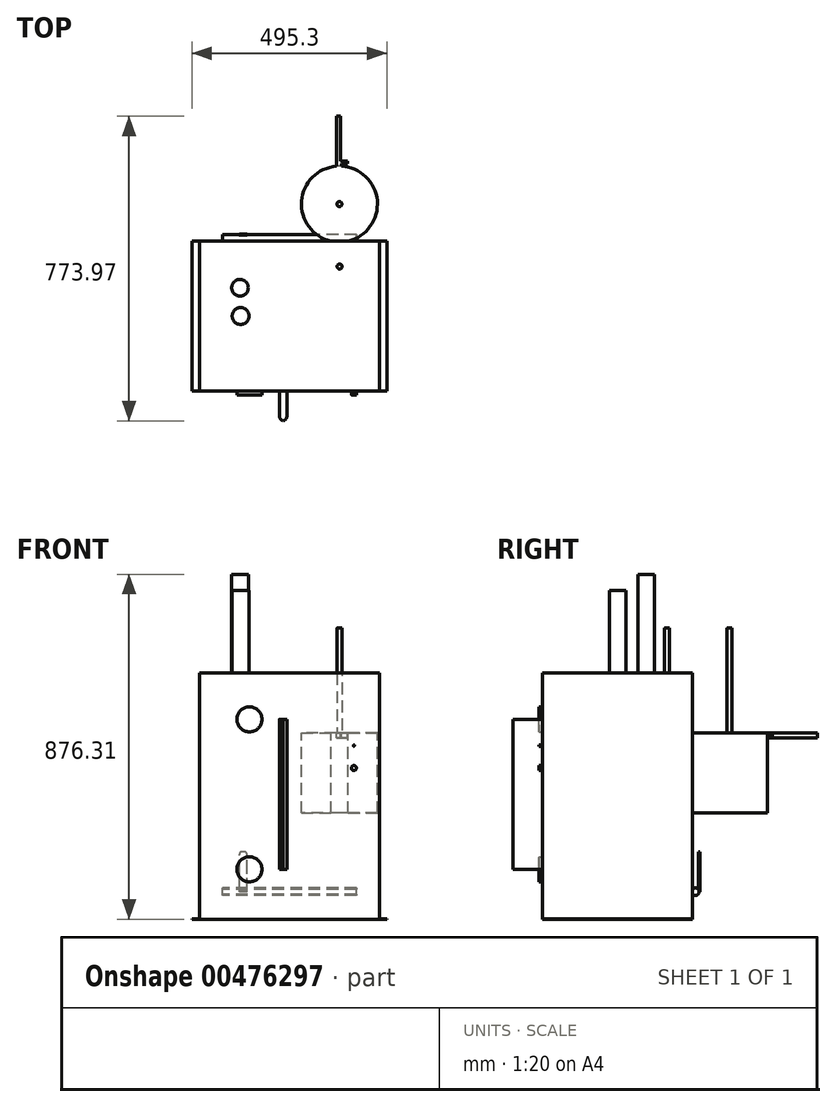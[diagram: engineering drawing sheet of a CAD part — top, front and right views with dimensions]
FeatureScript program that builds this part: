
annotation { "Feature Type Name" : "Feature", "Feature Type Description" : "" }
export const myFeature = defineFeature(function(context is Context, id is Id, definition is map)
    precondition{}
    {
        {
            var Q0;
            Q0=qCreatedBy(makeId("Top.planeOp"),FACE);
            var sketch = newSketch(context, id + "F0", { "sketchPlane" : qUnion([Q0])});
            skLineSegment(sketch, "E0.bottom", {"start": v(-228.6, 190.5) * mm, "end": v(228.6, 190.5) * mm});
            skLineSegment(sketch, "E0.top", {"start": v(-228.6, -190.5) * mm, "end": v(228.6, -190.5) * mm});
            skLineSegment(sketch, "E0.left", {"start": v(-228.6, 190.5) * mm, "end": v(-228.6, -190.5) * mm});
            skLineSegment(sketch, "E0.right", {"start": v(228.6, 190.5) * mm, "end": v(228.6, -190.5) * mm});
            skLineSegment(sketch, "E1", {"start": v(-228.6, 0) * mm, "end": v(228.6, 0) * mm, "construction": true});
            skPoint(sketch, "E2", {"position": v(0, 0) * mm});
            skSolve(sketch);
        }
        {
            var Q0;
            Q0 = qSketchRegion(id + "F0", true);
            extrude(context, id + "F1", {"entities" : qUnion([Q0]), "oppositeDirection" : true, "depth" : 625.47 * mm, "offsetDistance" : 25.4 * mm});
        }
        {
            var Q0;
            Q0=makeQuery(id+"F1.opExtrude","CAP_FACE",FACE,{"disambiguationData":[OSD([sQuery(id+"F0.wireOp",EDGE,"E0.bottom"),sQuery(id+"F0.wireOp",EDGE,"E0.top"),sQuery(id+"F0.wireOp",EDGE,"E0.left"),sQuery(id+"F0.wireOp",EDGE,"E0.right")])],"isStart":true});
            var sketch = newSketch(context, id + "F2", { "sketchPlane" : qUnion([Q0])});
            skCircle(sketch, "E3", {"center": v(-125.47, 72) * mm, "radius": 21.1 * mm});
            skSolve(sketch);
        }
        {
            var Q0;
            Q0 = qSketchRegion(id + "F2", true);
            extrude(context, id + "F3", {"entities" : qUnion([Q0]), "operationType" : NewBodyOperationType.ADD, "depth" : 250.82 * mm, "offsetDistance" : 25.4 * mm});
        }
        {
            var Q0;
            Q0=makeQuery(id+"F1.opExtrude","CAP_FACE",FACE,{"disambiguationData":[OSD([sQuery(id+"F0.wireOp",EDGE,"E0.bottom"),sQuery(id+"F0.wireOp",EDGE,"E0.top"),sQuery(id+"F0.wireOp",EDGE,"E0.left"),sQuery(id+"F0.wireOp",EDGE,"E0.right")])],"isStart":true});
            var sketch = newSketch(context, id + "F4", { "sketchPlane" : qUnion([Q0])});
            skCircle(sketch, "E4", {"center": v(-124.02, 0) * mm, "radius": 21.4 * mm});
            skSolve(sketch);
        }
        {
            var Q0;
            Q0 = qSketchRegion(id + "F4", true);
            extrude(context, id + "F5", {"entities" : qUnion([Q0]), "operationType" : NewBodyOperationType.ADD, "depth" : 209.55 * mm, "offsetDistance" : 25.4 * mm});
        }
        {
            var Q0;
            Q0=makeQuery(id+"F1.opExtrude","SWEPT_FACE",FACE,{"disambiguationData":[OSD([sQuery(id+"F0.wireOp",EDGE,"E0.top")])]});
            var sketch = newSketch(context, id + "F6", { "sketchPlane" : qUnion([Q0])});
            skCircle(sketch, "E5", {"center": v(-101.6, -117.48) * mm, "radius": 31.75 * mm});
            skCircle(sketch, "E6", {"center": v(-101.6, -498.48) * mm, "radius": 31.75 * mm});
            skCircle(sketch, "E7", {"center": v(163.79, -184.2) * mm, "radius": 1.59 * mm});
            skLineSegment(sketch, "E8", {"start": v(163.79, -184.2) * mm, "end": v(163.79, -241.12) * mm, "construction": true});
            skCircle(sketch, "E9", {"center": v(163.79, -241.12) * mm, "radius": 6.35 * mm});
            skSolve(sketch);
        }
        {
            var Q0;
            Q0 = qSketchRegion(id + "F6", true);
            extrude(context, id + "F7", {"entities" : qUnion([Q0]), "operationType" : NewBodyOperationType.ADD, "depth" : 9.52 * mm, "offsetDistance" : 25.4 * mm});
        }
        {
            var Q0;
            Q0=makeQuery(id+"F1.opExtrude","SWEPT_FACE",FACE,{"disambiguationData":[OSD([sQuery(id+"F0.wireOp",EDGE,"E0.top")])]});
            var sketch = newSketch(context, id + "F8", { "sketchPlane" : qUnion([Q0])});
            skLineSegment(sketch, "E10.bottom", {"start": v(-25.4, -117.48) * mm, "end": v(-6.35, -117.48) * mm});
            skLineSegment(sketch, "E10.top", {"start": v(-25.4, -498.48) * mm, "end": v(-6.35, -498.48) * mm});
            skLineSegment(sketch, "E10.left", {"start": v(-25.4, -117.48) * mm, "end": v(-25.4, -498.48) * mm});
            skLineSegment(sketch, "E10.right", {"start": v(-6.35, -117.48) * mm, "end": v(-6.35, -498.48) * mm});
            skPoint(sketch, "E11", {"position": v(-101.6, -117.48) * mm});
            skPoint(sketch, "E12", {"position": v(-101.6, -498.48) * mm});
            skSolve(sketch);
        }
        {
            var Q0;
            Q0 = qSketchRegion(id + "F8", true);
            extrude(context, id + "F9", {"entities" : qUnion([Q0]), "operationType" : NewBodyOperationType.ADD, "depth" : 76.2 * mm, "offsetDistance" : 25.4 * mm});
        }
        {
            var Q0;
            Q0=makeQuery(id+"F9.opExtrude","CAP_EDGE",EDGE,{"disambiguationData":[OSD([sQuery(id+"F8.wireOp",EDGE,"E10.left")])],"isStart":false});
            var Q1;
            Q1=makeQuery(id+"F9.opExtrude","CAP_EDGE",EDGE,{"disambiguationData":[OSD([sQuery(id+"F8.wireOp",EDGE,"E10.right")])],"isStart":false});
            fillet(context, id + "F10", {"entities" : qUnion([Q0, Q1]), "radius" : 12.7 * mm, "tangentPropagation" : true, "allowEdgeOverflow" : false});
        }
        {
            var Q0;
            Q0=qCreatedBy(makeId("Top.planeOp"),FACE);
            cPlane(context, id + "F11", {"entities" : qUnion([Q0]), "cplaneType" : CPlaneType.OFFSET, "offset" : 152.4 * mm, "oppositeDirection" : true, "width" : 152.4 * mm, "height" : 152.4 * mm});
        }
        {
            var Q0;
            Q0=qCreatedBy(id+"F11.planeOp",FACE);
            var sketch = newSketch(context, id + "F12", { "sketchPlane" : qUnion([Q0])});
            skCircle(sketch, "E13", {"center": v(127.07, 284.48) * mm, "radius": 96.52 * mm});
            skLineSegment(sketch, "E14", {"start": v(127.07, 381) * mm, "end": v(127.07, 187.96) * mm, "construction": true});
            skSolve(sketch);
        }
        {
            var Q0;
            Q0 = qSketchRegion(id + "F12", true);
            extrude(context, id + "F13", {"entities" : qUnion([Q0]), "operationType" : NewBodyOperationType.ADD, "oppositeDirection" : true, "depth" : 203.2 * mm, "offsetDistance" : 25.4 * mm});
        }
        {
            var Q0;
            Q0=makeQuery(id+"F13.opExtrude","CAP_FACE",FACE,{"disambiguationData":[OSD([sQuery(id+"F12.wireOp",EDGE,"E13")])],"isStart":true});
            var sketch = newSketch(context, id + "F14", { "sketchPlane" : qUnion([Q0])});
            skLineSegment(sketch, "E15", {"start": v(119.09, 380.67) * mm, "end": v(119.09, 393.37) * mm});
            skLineSegment(sketch, "E16", {"start": v(129.25, 393.37) * mm, "end": v(147.66, 393.37) * mm});
            skLineSegment(sketch, "E17", {"start": v(147.66, 393.37) * mm, "end": v(147.66, 387.02) * mm});
            skLineSegment(sketch, "E18", {"start": v(147.66, 387.02) * mm, "end": v(131.79, 387.02) * mm});
            skLineSegment(sketch, "E19", {"start": v(131.79, 387.02) * mm, "end": v(131.79, 380.88) * mm});
            skLineSegment(sketch, "E20", {"start": v(119.09, 380.67) * mm, "end": v(131.79, 380.88) * mm});
            skLineSegment(sketch, "E21", {"start": v(119.09, 393.37) * mm, "end": v(119.09, 507.67) * mm});
            skLineSegment(sketch, "E22", {"start": v(119.09, 507.67) * mm, "end": v(129.25, 507.67) * mm});
            skLineSegment(sketch, "E23", {"start": v(129.25, 507.67) * mm, "end": v(129.25, 393.37) * mm});
            skSolve(sketch);
        }
        {
            var Q0;
            Q0 = qSketchRegion(id + "F14", true);
            extrude(context, id + "F15", {"entities" : qUnion([Q0]), "operationType" : NewBodyOperationType.ADD, "oppositeDirection" : true, "depth" : 12.7 * mm, "offsetDistance" : 25.4 * mm});
        }
        {
            var Q0;
            Q0=makeQuery(id+"F15.boolean.opBoolean","MERGE",FACE,{"derivedFrom":[makeQuery(id+"F13.opExtrude","CAP_FACE",FACE,{"disambiguationData":[OSD([sQuery(id+"F12.wireOp",EDGE,"E13")])],"isStart":true}),makeQuery(id+"F15.opExtrude","CAP_FACE",FACE,{"disambiguationData":[OSD([sQuery(id+"F14.wireOp",EDGE,"E15"),sQuery(id+"F14.wireOp",EDGE,"E16"),sQuery(id+"F14.wireOp",EDGE,"E17"),sQuery(id+"F14.wireOp",EDGE,"E18"),sQuery(id+"F14.wireOp",EDGE,"E19"),sQuery(id+"F14.wireOp",EDGE,"E20"),sQuery(id+"F14.wireOp",EDGE,"E21"),sQuery(id+"F14.wireOp",EDGE,"E22"),sQuery(id+"F14.wireOp",EDGE,"E23")])],"isStart":true})]});
            var sketch = newSketch(context, id + "F16", { "sketchPlane" : qUnion([Q0])});
            skCircle(sketch, "E24", {"center": v(127.07, 284.48) * mm, "radius": 6.35 * mm});
            skSolve(sketch);
        }
        {
            var Q0;
            Q0 = qSketchRegion(id + "F16", true);
            extrude(context, id + "F17", {"entities" : qUnion([Q0]), "operationType" : NewBodyOperationType.ADD, "depth" : 266.7 * mm, "offsetDistance" : 25.4 * mm});
        }
        {
            var Q0;
            Q0=makeQuery(id+"F1.opExtrude","CAP_FACE",FACE,{"disambiguationData":[OSD([sQuery(id+"F0.wireOp",EDGE,"E0.bottom"),sQuery(id+"F0.wireOp",EDGE,"E0.top"),sQuery(id+"F0.wireOp",EDGE,"E0.left"),sQuery(id+"F0.wireOp",EDGE,"E0.right")])],"isStart":true});
            var sketch = newSketch(context, id + "F18", { "sketchPlane" : qUnion([Q0])});
            skLineSegment(sketch, "E25", {"start": v(127.43, 278.14) * mm, "end": v(127.43, 125.74) * mm, "construction": true});
            skCircle(sketch, "E26", {"center": v(127.43, 125.74) * mm, "radius": 6.35 * mm});
            skSolve(sketch);
        }
        {
            var Q0;
            Q0 = qSketchRegion(id + "F18", true);
            extrude(context, id + "F19", {"entities" : qUnion([Q0]), "operationType" : NewBodyOperationType.ADD, "depth" : 114.3 * mm, "offsetDistance" : 25.4 * mm});
        }
        {
            var Q0;
            Q0=qCreatedBy(makeId("Right.planeOp"),FACE);
            var sketch = newSketch(context, id + "F20", { "sketchPlane" : qUnion([Q0])});
            skCircle(sketch, "E27", {"center": v(197.49, -555.63) * mm, "radius": 9.53 * mm});
            skLineSegment(sketch, "E28", {"start": v(197.49, -555.63) * mm, "end": v(190.5, -555.63) * mm, "construction": true});
            skLineSegment(sketch, "E29", {"start": v(190.5, -555.63) * mm, "end": v(187.96, -555.63) * mm, "construction": true});
            skSolve(sketch);
        }
        {
            var Q0;
            Q0 = qSketchRegion(id + "F20", true);
            extrude(context, id + "F21", {"entities" : qUnion([Q0]), "operationType" : NewBodyOperationType.ADD, "endBound" : BoundingType.SYMMETRIC, "depth" : 340.36 * mm, "offsetDistance" : 25.4 * mm});
        }
        {
            var Q0;
            Q0=makeQuery(id+"F1.opExtrude","SWEPT_FACE",FACE,{"disambiguationData":[OSD([sQuery(id+"F0.wireOp",EDGE,"E0.left")])]});
            var sketch = newSketch(context, id + "F22", { "sketchPlane" : qUnion([Q0])});
            skLineSegment(sketch, "E30.bottom", {"start": v(-190.5, -625.48) * mm, "end": v(190.5, -625.48) * mm});
            skLineSegment(sketch, "E30.top", {"start": v(-190.5, -624.2) * mm, "end": v(190.5, -624.2) * mm});
            skLineSegment(sketch, "E30.left", {"start": v(-190.5, -625.48) * mm, "end": v(-190.5, -624.2) * mm});
            skLineSegment(sketch, "E30.right", {"start": v(190.5, -625.48) * mm, "end": v(190.5, -624.2) * mm});
            skSolve(sketch);
        }
        {
            var Q0;
            Q0 = qSketchRegion(id + "F22", true);
            extrude(context, id + "F23", {"entities" : qUnion([Q0]), "operationType" : NewBodyOperationType.ADD, "depth" : 19.05 * mm, "offsetDistance" : 25.4 * mm});
        }
        {
            var Q0;
            Q0=makeQuery(id+"F1.opExtrude","SWEPT_FACE",FACE,{"disambiguationData":[OSD([sQuery(id+"F0.wireOp",EDGE,"E0.right")])]});
            var sketch = newSketch(context, id + "F24", { "sketchPlane" : qUnion([Q0])});
            skLineSegment(sketch, "E31.bottom", {"start": v(-190.5, -625.48) * mm, "end": v(190.5, -625.48) * mm});
            skLineSegment(sketch, "E31.top", {"start": v(-190.5, -624.2) * mm, "end": v(190.5, -624.2) * mm});
            skLineSegment(sketch, "E31.left", {"start": v(-190.5, -625.48) * mm, "end": v(-190.5, -624.2) * mm});
            skLineSegment(sketch, "E31.right", {"start": v(190.5, -625.48) * mm, "end": v(190.5, -624.2) * mm});
            skSolve(sketch);
        }
        {
            var Q0;
            Q0 = qSketchRegion(id + "F24", true);
            extrude(context, id + "F25", {"entities" : qUnion([Q0]), "operationType" : NewBodyOperationType.ADD, "depth" : 19.05 * mm, "offsetDistance" : 25.4 * mm});
        }
        {
            var Q0;
            Q0=qCreatedBy(makeId("Front.planeOp"),FACE);
            cPlane(context, id + "F26", {"entities" : qUnion([Q0]), "cplaneType" : CPlaneType.OFFSET, "offset" : 205.74 * mm, "oppositeDirection" : true, "width" : 152.4 * mm, "height" : 152.4 * mm});
        }
        {
            var Q0;
            Q0=qCreatedBy(id+"F26.planeOp",FACE);
            var sketch = newSketch(context, id + "F27", { "sketchPlane" : qUnion([Q0])});
            skLineSegment(sketch, "E32.bottom", {"start": v(-107.95, -555.63) * mm, "end": v(-127, -555.63) * mm});
            skLineSegment(sketch, "E32.top", {"start": v(-114.3, -454.03) * mm, "end": v(-120.65, -454.03) * mm});
            skLineSegment(sketch, "E32.left", {"start": v(-107.95, -555.63) * mm, "end": v(-107.95, -460.38) * mm});
            skLineSegment(sketch, "E32.right", {"start": v(-127, -555.63) * mm, "end": v(-127, -460.38) * mm});
            skLineSegment(sketch, "E33", {"start": v(-170.18, -555.63) * mm, "end": v(170.18, -555.63) * mm, "construction": true});
            skPoint(sketch, "E34.visualSharp", {"position": v(-107.95, -454.03) * mm});
            skArc(sketch, "E34.filletArc", {"start": v(-107.95, -460.38) * mm, "mid": v(-109.8, -455.88) * mm, "end": v(-114.3, -454.03) * mm});
            skPoint(sketch, "E35.visualSharp", {"position": v(-127, -454.03) * mm});
            skArc(sketch, "E35.filletArc", {"start": v(-120.65, -454.03) * mm, "mid": v(-125.14, -455.88) * mm, "end": v(-127, -460.38) * mm});
            skSolve(sketch);
        }
        {
            var Q0;
            Q0 = qSketchRegion(id + "F27", true);
            extrude(context, id + "F28", {"entities" : qUnion([Q0]), "operationType" : NewBodyOperationType.ADD, "oppositeDirection" : true, "depth" : 3.17 * mm, "offsetDistance" : 25.4 * mm});
        }
    });
